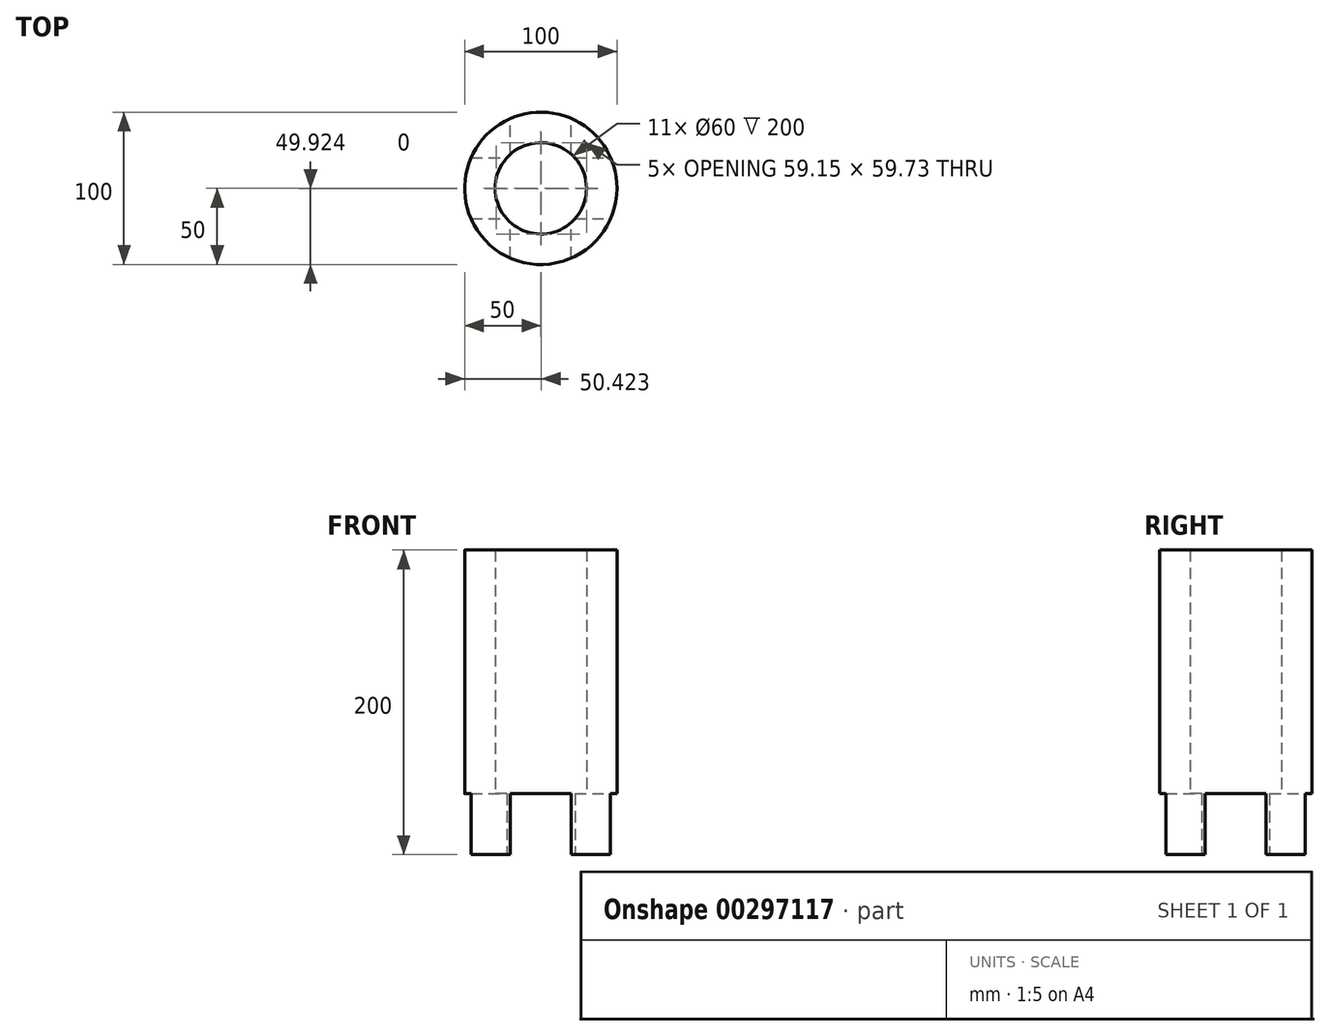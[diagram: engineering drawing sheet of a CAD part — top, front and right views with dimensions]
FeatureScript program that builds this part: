
annotation { "Feature Type Name" : "Feature", "Feature Type Description" : "" }
export const myFeature = defineFeature(function(context is Context, id is Id, definition is map)
    precondition{}
    {
        {
            var Q0;
            Q0=qCreatedBy(makeId("Top.planeOp"),FACE);
            var sketch = newSketch(context, id + "F0", { "sketchPlane" : qUnion([Q0])});
            skCircle(sketch, "E0", {"center": v(0, 0) * mm, "radius": 30 * mm});
            skCircle(sketch, "E1", {"center": v(0, 0) * mm, "radius": 50 * mm});
            skSolve(sketch);
        }
        {
            var Q0;
            Q0 = qSketchRegion(id + "F0", true);
            extrude(context, id + "F1", {"entities" : qUnion([Q0]), "depth" : 200 * mm});
        }
        {
            var Q0;
            Q0=qCreatedBy(makeId("Front.planeOp"),FACE);
            var sketch = newSketch(context, id + "F2", { "sketchPlane" : qUnion([Q0])});
            skLineSegment(sketch, "E2.bottom", {"start": v(20, 40) * mm, "end": v(-20, 40) * mm});
            skLineSegment(sketch, "E2.top", {"start": v(20, -40) * mm, "end": v(-20, -40) * mm});
            skLineSegment(sketch, "E2.left", {"start": v(20, 40) * mm, "end": v(20, -40) * mm});
            skLineSegment(sketch, "E2.right", {"start": v(-20, 40) * mm, "end": v(-20, -40) * mm});
            skPoint(sketch, "E2.middle", {"position": v(0, 0) * mm});
            skSolve(sketch);
        }
        {
            var Q0;
            Q0 = qSketchRegion(id + "F2", true);
            extrude(context, id + "F3", {"entities" : qUnion([Q0]), "operationType" : NewBodyOperationType.REMOVE, "endBound" : BoundingType.SYMMETRIC, "depth" : 9900 * mm});
        }
        {
            var Q0;
            Q0=qCreatedBy(makeId("Right.planeOp"),FACE);
            var sketch = newSketch(context, id + "F4", { "sketchPlane" : qUnion([Q0])});
            skLineSegment(sketch, "E3.bottom", {"start": v(-20, 40) * mm, "end": v(20, 40) * mm});
            skLineSegment(sketch, "E3.top", {"start": v(-20, -40) * mm, "end": v(20, -40) * mm});
            skLineSegment(sketch, "E3.left", {"start": v(-20, 40) * mm, "end": v(-20, -40) * mm});
            skLineSegment(sketch, "E3.right", {"start": v(20, 40) * mm, "end": v(20, -40) * mm});
            skPoint(sketch, "E3.middle", {"position": v(0, 0) * mm});
            skSolve(sketch);
        }
        {
            var Q0;
            Q0 = qSketchRegion(id + "F4", true);
            extrude(context, id + "F5", {"entities" : qUnion([Q0]), "operationType" : NewBodyOperationType.REMOVE, "endBound" : BoundingType.SYMMETRIC, "oppositeDirection" : true, "depth" : 5678 * mm});
        }
    });
